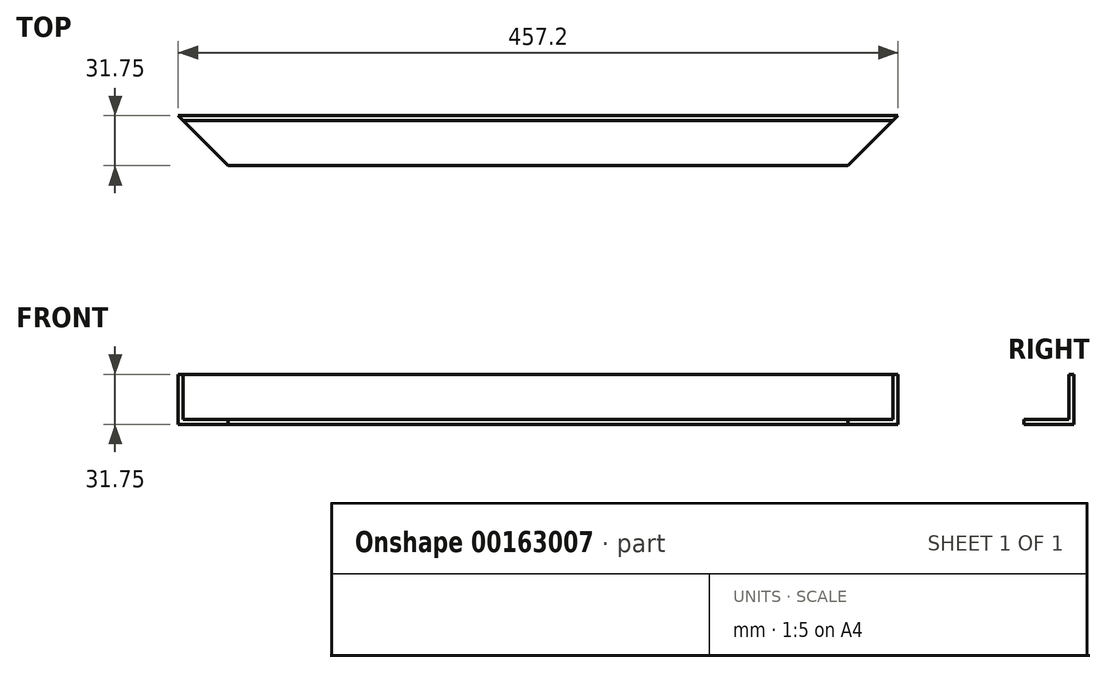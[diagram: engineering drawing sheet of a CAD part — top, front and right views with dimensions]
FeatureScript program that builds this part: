
annotation { "Feature Type Name" : "Feature", "Feature Type Description" : "" }
export const myFeature = defineFeature(function(context is Context, id is Id, definition is map)
    precondition{}
    {
        {
            var Q0;
            Q0=qCreatedBy(makeId("Right.planeOp"),FACE);
            var sketch = newSketch(context, id + "F0", { "sketchPlane" : qUnion([Q0])});
            skLineSegment(sketch, "E0", {"start": v(0, 0) * mm, "end": v(0, 31.75) * mm});
            skLineSegment(sketch, "E1", {"start": v(0, 0) * mm, "end": v(-31.75, 0) * mm});
            skLineSegment(sketch, "E2", {"start": v(-31.75, 0) * mm, "end": v(-31.75, 3.17) * mm});
            skLineSegment(sketch, "E3", {"start": v(-31.75, 3.17) * mm, "end": v(-3.17, 3.17) * mm});
            skLineSegment(sketch, "E4", {"start": v(-3.17, 3.17) * mm, "end": v(-3.17, 31.75) * mm});
            skLineSegment(sketch, "E5", {"start": v(-3.17, 31.75) * mm, "end": v(0, 31.75) * mm});
            skSolve(sketch);
        }
        {
            var Q0;
            Q0=qSketchRegion(id+"F0",true);
            extrude(context, id + "F1", {"entities" : qUnion([Q0]), "depth" : 457.2 * mm});
        }
        {
            var Q0;
            Q0=qCreatedBy(makeId("Right.planeOp"),FACE);
            var Q1;
            Q1=makeQuery(id+"F1.opExtrude","CAP_EDGE",EDGE,{"disambiguationData":[OSD([sQuery(id+"F0.wireOp",EDGE,"E0")])],"isStart":true});
            cPlane(context, id + "F2", {"entities" : qUnion([Q0, Q1]), "cplaneType" : CPlaneType.LINE_ANGLE, "offset" : 25.4 * mm, "angle" : 45 * degree, "width" : 152.4 * mm, "height" : 152.4 * mm});
        }
        {
            var Q0;
            Q0=makeQuery(id+"F1.opExtrude","CAP_FACE",FACE,{"disambiguationData":[OSD([sQuery(id+"F0.wireOp",EDGE,"E0"),sQuery(id+"F0.wireOp",EDGE,"E1"),sQuery(id+"F0.wireOp",EDGE,"E2"),sQuery(id+"F0.wireOp",EDGE,"E3"),sQuery(id+"F0.wireOp",EDGE,"E4"),sQuery(id+"F0.wireOp",EDGE,"E5")])],"isStart":true});
            var Q1;
            Q1=qCreatedBy(id+"F2.planeOp",FACE);
            extrude(context, id + "F3", {"entities" : qUnion([Q0]), "operationType" : NewBodyOperationType.REMOVE, "endBound" : BoundingType.UP_TO_SURFACE, "oppositeDirection" : true, "endBoundEntityFace" : qUnion([Q1]), "depth" : 25.4 * mm});
        }
        {
            var Q0;
            Q0=makeQuery(id+"F1.opExtrude","CAP_EDGE",EDGE,{"disambiguationData":[OSD([sQuery(id+"F0.wireOp",EDGE,"E0")])],"isStart":false});
            cPlane(context, id + "F4", {"entities" : qUnion([Q0]), "cplaneType" : CPlaneType.LINE_ANGLE, "offset" : 25.4 * mm, "angle" : 315 * degree, "width" : 152.4 * mm, "height" : 152.4 * mm});
        }
        {
            var Q0;
            Q0=makeQuery(id+"F1.opExtrude","CAP_FACE",FACE,{"disambiguationData":[OSD([sQuery(id+"F0.wireOp",EDGE,"E0"),sQuery(id+"F0.wireOp",EDGE,"E1"),sQuery(id+"F0.wireOp",EDGE,"E2"),sQuery(id+"F0.wireOp",EDGE,"E3"),sQuery(id+"F0.wireOp",EDGE,"E4"),sQuery(id+"F0.wireOp",EDGE,"E5")])],"isStart":false});
            var Q1;
            Q1=qCreatedBy(id+"F4.planeOp",FACE);
            extrude(context, id + "F5", {"entities" : qUnion([Q0]), "operationType" : NewBodyOperationType.REMOVE, "endBound" : BoundingType.UP_TO_SURFACE, "oppositeDirection" : true, "endBoundEntityFace" : qUnion([Q1]), "depth" : 25.4 * mm});
        }
    });
